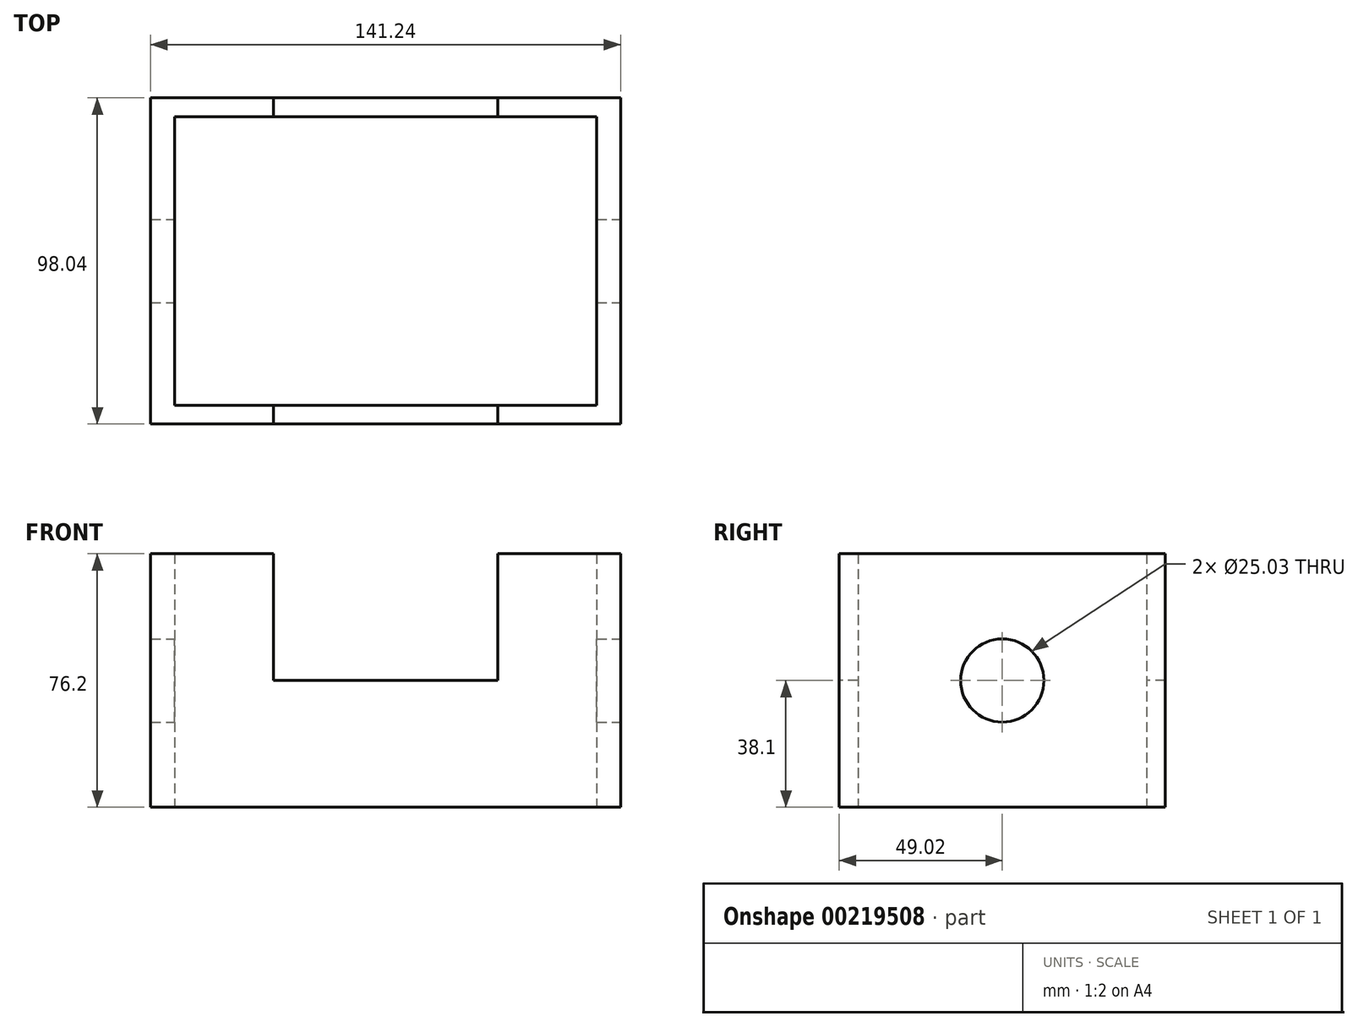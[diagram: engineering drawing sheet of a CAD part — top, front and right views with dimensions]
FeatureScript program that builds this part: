
annotation { "Feature Type Name" : "Feature", "Feature Type Description" : "" }
export const myFeature = defineFeature(function(context is Context, id is Id, definition is map)
    precondition{}
    {
        {
            var Q0;
            Q0=qCreatedBy(makeId("Top.planeOp"),FACE);
            var sketch = newSketch(context, id + "F0", { "sketchPlane" : qUnion([Q0])});
            skLineSegment(sketch, "E0.bottom", {"start": v(70.62, 49.02) * mm, "end": v(-70.62, 49.02) * mm});
            skLineSegment(sketch, "E0.top", {"start": v(70.62, -49.02) * mm, "end": v(-70.62, -49.02) * mm});
            skLineSegment(sketch, "E0.left", {"start": v(70.62, 49.02) * mm, "end": v(70.62, -49.02) * mm});
            skLineSegment(sketch, "E0.right", {"start": v(-70.62, 49.02) * mm, "end": v(-70.62, -49.02) * mm});
            skPoint(sketch, "E0.middle", {"position": v(0, 0) * mm});
            skLineSegment(sketch, "E1.bottom", {"start": v(63.47, 43.36) * mm, "end": v(-63.47, 43.36) * mm});
            skLineSegment(sketch, "E1.top", {"start": v(63.47, -43.36) * mm, "end": v(-63.47, -43.36) * mm});
            skLineSegment(sketch, "E1.left", {"start": v(63.47, 43.36) * mm, "end": v(63.47, -43.36) * mm});
            skLineSegment(sketch, "E1.right", {"start": v(-63.47, 43.36) * mm, "end": v(-63.47, -43.36) * mm});
            skSolve(sketch);
        }
        {
            var Q0;
            Q0 = qSketchRegion(id + "F0", true);
            extrude(context, id + "F1", {"entities" : qUnion([Q0]), "depth" : 76.2 * mm});
        }
        {
            var Q0;
            Q0=makeQuery(id+"F1.opExtrude","SWEPT_FACE",FACE,{"disambiguationData":[OSD([sQuery(id+"F0.wireOp",EDGE,"E0.left")])]});
            var sketch = newSketch(context, id + "F2", { "sketchPlane" : qUnion([Q0])});
            skCircle(sketch, "E2", {"center": v(0, 38.1) * mm, "radius": 12.51 * mm});
            skPoint(sketch, "E2.centerSnap0", {"position": v(49.02, 38.1) * mm});
            skPoint(sketch, "E2.centerSnap1", {"position": v(0, 76.2) * mm});
            skSolve(sketch);
        }
        {
            var Q0;
            Q0 = qSketchRegion(id + "F2", true);
            extrude(context, id + "F3", {"entities" : qUnion([Q0]), "operationType" : NewBodyOperationType.REMOVE, "oppositeDirection" : true, "depth" : 255.78 * mm});
        }
        {
            var Q0;
            Q0=makeQuery(id+"F1.opExtrude","SWEPT_FACE",FACE,{"disambiguationData":[OSD([sQuery(id+"F0.wireOp",EDGE,"E0.top")])]});
            var sketch = newSketch(context, id + "F4", { "sketchPlane" : qUnion([Q0])});
            skLineSegment(sketch, "E3.bottom", {"start": v(-33.67, 76.2) * mm, "end": v(33.67, 76.2) * mm});
            skLineSegment(sketch, "E3.top", {"start": v(-33.67, 38.1) * mm, "end": v(33.67, 38.1) * mm});
            skLineSegment(sketch, "E3.left", {"start": v(-33.67, 76.2) * mm, "end": v(-33.67, 38.1) * mm});
            skLineSegment(sketch, "E3.right", {"start": v(33.67, 76.2) * mm, "end": v(33.67, 38.1) * mm});
            skPoint(sketch, "E3.middle", {"position": v(0, 57.15) * mm});
            skSolve(sketch);
        }
        {
            var Q0;
            Q0 = qSketchRegion(id + "F4", true);
            extrude(context, id + "F5", {"entities" : qUnion([Q0]), "operationType" : NewBodyOperationType.REMOVE, "oppositeDirection" : true, "depth" : 172.47 * mm});
        }
    });
